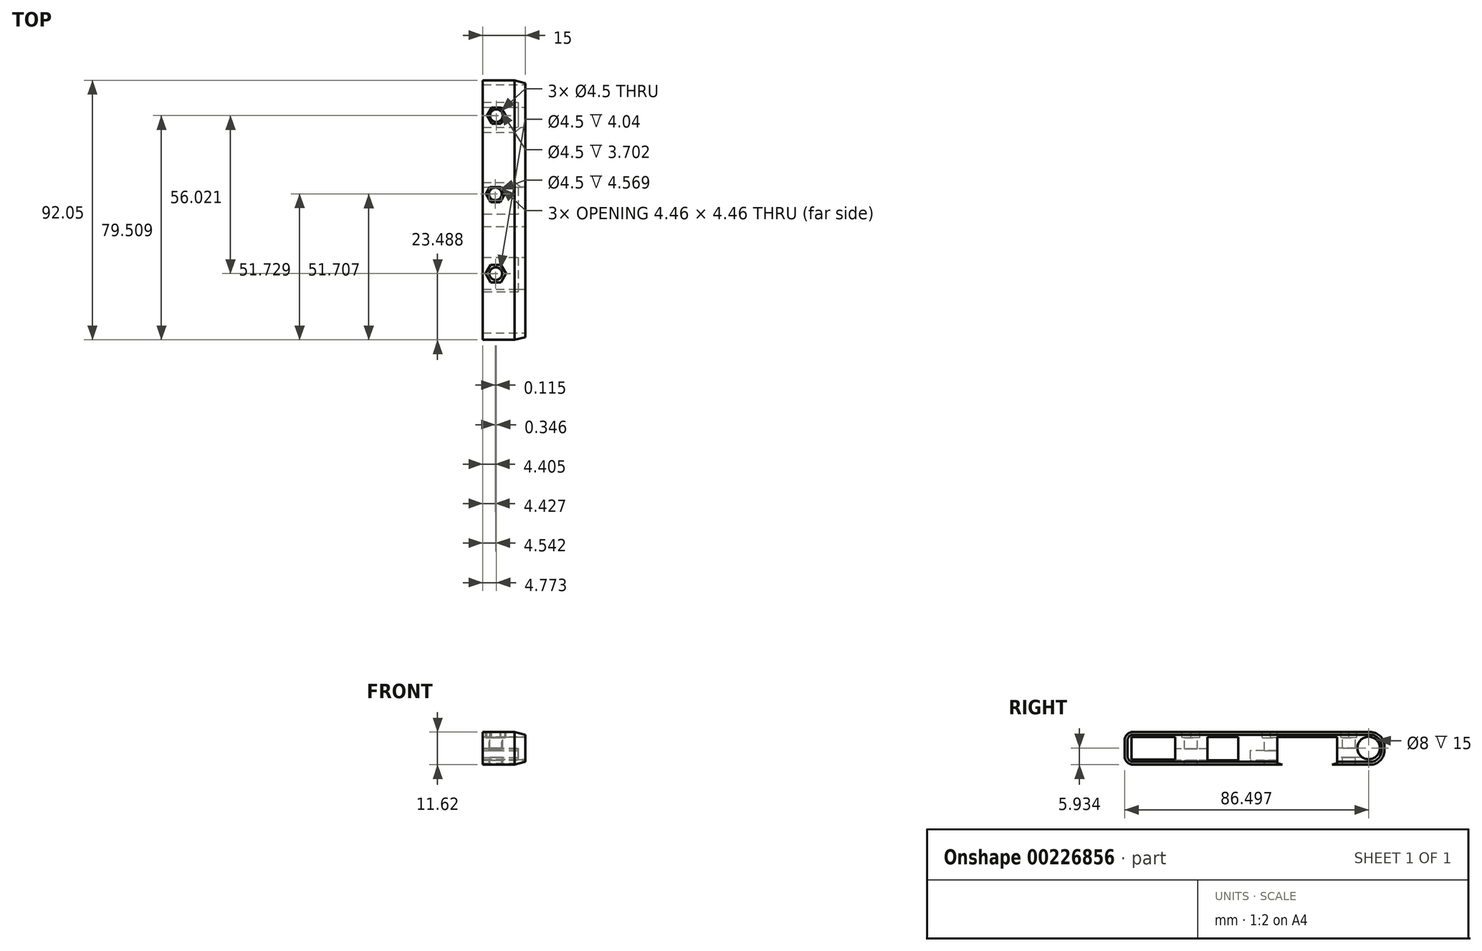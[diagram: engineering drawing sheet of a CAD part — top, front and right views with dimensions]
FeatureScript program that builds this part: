
annotation { "Feature Type Name" : "Feature", "Feature Type Description" : "" }
export const myFeature = defineFeature(function(context is Context, id is Id, definition is map)
    precondition{}
    {
        {
            var Q0;
            Q0=qCreatedBy(makeId("Right.planeOp"),FACE);
            var sketch = newSketch(context, id + "F0", { "sketchPlane" : qUnion([Q0])});
            skLineSegment(sketch, "E0.bottom", {"start": v(42.33, 35.55) * mm, "end": v(-49.72, 35.55) * mm});
            skLineSegment(sketch, "E0.top", {"start": v(42.33, 23.93) * mm, "end": v(-49.72, 23.93) * mm});
            skLineSegment(sketch, "E0.left", {"start": v(42.33, 35.55) * mm, "end": v(42.33, 23.93) * mm});
            skLineSegment(sketch, "E0.right", {"start": v(-49.72, 35.55) * mm, "end": v(-49.72, 23.93) * mm});
            skLineSegment(sketch, "E1.bottom", {"start": v(-31.82, 33.8) * mm, "end": v(-47.32, 33.8) * mm});
            skLineSegment(sketch, "E1.top", {"start": v(-31.82, 25.7) * mm, "end": v(-47.32, 25.7) * mm});
            skLineSegment(sketch, "E1.left", {"start": v(-31.82, 33.8) * mm, "end": v(-31.82, 25.7) * mm});
            skLineSegment(sketch, "E1.right", {"start": v(-47.32, 33.8) * mm, "end": v(-47.32, 25.7) * mm});
            skLineSegment(sketch, "E2.bottom", {"start": v(25.58, 33.8) * mm, "end": v(4.38, 33.8) * mm});
            skLineSegment(sketch, "E2.top", {"start": v(25.58, 23.5) * mm, "end": v(4.38, 23.5) * mm});
            skLineSegment(sketch, "E2.left", {"start": v(25.58, 33.8) * mm, "end": v(25.58, 23.5) * mm});
            skLineSegment(sketch, "E2.right", {"start": v(4.38, 33.8) * mm, "end": v(4.38, 23.5) * mm});
            skCircle(sketch, "E3", {"center": v(36.78, 29.86) * mm, "radius": 4 * mm});
            skLineSegment(sketch, "E4.bottom", {"start": v(-9.52, 33.8) * mm, "end": v(-20.42, 33.8) * mm});
            skLineSegment(sketch, "E4.top", {"start": v(-9.52, 25.5) * mm, "end": v(-20.42, 25.5) * mm});
            skLineSegment(sketch, "E4.left", {"start": v(-9.52, 33.8) * mm, "end": v(-9.52, 25.5) * mm});
            skLineSegment(sketch, "E4.right", {"start": v(-20.42, 33.8) * mm, "end": v(-20.42, 25.5) * mm});
            skLineSegment(sketch, "E5", {"start": v(25.58, 24.5) * mm, "end": v(22.58, 23.5) * mm});
            skLineSegment(sketch, "E6", {"start": v(14.98, 23.5) * mm, "end": v(14.98, 33.8) * mm, "construction": true});
            skLineSegment(sketch, "E7.MirrorCS", {"start": v(4.38, 24.5) * mm, "end": v(7.38, 23.5) * mm});
            skLineSegment(sketch, "E8", {"start": v(25.58, 33.8) * mm, "end": v(37.44, 33.8) * mm, "construction": true});
            skLineSegment(sketch, "E9", {"start": v(4.38, 33.8) * mm, "end": v(-9.52, 33.8) * mm, "construction": true});
            skLineSegment(sketch, "E10", {"start": v(-31.82, 33.8) * mm, "end": v(-20.42, 33.8) * mm, "construction": true});
            skSolve(sketch);
        }
        {
            var Q0;
            Q0=makeQuery(id+"F0.imprint","IMPRINT",FACE,{"disambiguationData":[TD([[makeQuery(id+"F0.imprint","IMPRINT",EDGE,{"derivedFrom":sQuery(id+"F0.wireOp",EDGE,"E0.bottom")}),1.0]])]});
            var Q1;
            {var subQ3=sQuery(id+"F0.wireOp",EDGE,"E7.MirrorCS");Q1=makeQuery(id+"F0.imprint","IMPRINT",FACE,{"disambiguationData":[TD([[makeQuery(id+"F0.imprint","IMPRINT",EDGE,{"derivedFrom":subQ3}),-1.0]])]});}
            var Q2;
            {var subQ3=sQuery(id+"F0.wireOp",EDGE,"E5");Q2=makeQuery(id+"F0.imprint","IMPRINT",FACE,{"disambiguationData":[TD([[makeQuery(id+"F0.imprint","IMPRINT",EDGE,{"derivedFrom":subQ3}),1.0]])]});}
            extrude(context, id + "F1", {"entities" : qUnion([Q0, Q1, Q2]), "oppositeDirection" : true, "depth" : 15 * mm});
        }
        {
            var Q0;
            Q0=makeQuery(id+"F1.opExtrude","CAP_FACE",FACE,{"disambiguationData":[OSD([sQuery(id+"F0.wireOp",EDGE,"E0.bottom"),sQuery(id+"F0.wireOp",EDGE,"E0.top"),sQuery(id+"F0.wireOp",EDGE,"E0.left"),sQuery(id+"F0.wireOp",EDGE,"E0.right"),sQuery(id+"F0.wireOp",EDGE,"E1.bottom"),sQuery(id+"F0.wireOp",EDGE,"E1.top"),sQuery(id+"F0.wireOp",EDGE,"E1.left"),sQuery(id+"F0.wireOp",EDGE,"E1.right"),sQuery(id+"F0.wireOp",EDGE,"E2.bottom"),sQuery(id+"F0.wireOp",EDGE,"E2.top"),sQuery(id+"F0.wireOp",EDGE,"E2.left"),sQuery(id+"F0.wireOp",EDGE,"E2.right"),sQuery(id+"F0.wireOp",EDGE,"E3"),sQuery(id+"F0.wireOp",EDGE,"E4.bottom"),sQuery(id+"F0.wireOp",EDGE,"E4.top"),sQuery(id+"F0.wireOp",EDGE,"E4.left"),sQuery(id+"F0.wireOp",EDGE,"E4.right"),sQuery(id+"F0.wireOp",EDGE,"E5"),sQuery(id+"F0.wireOp",EDGE,"E7.MirrorCS")])],"isStart":false});
            var sketch = newSketch(context, id + "F2", { "sketchPlane" : qUnion([Q0])});
            skLineSegment(sketch, "E11.bottom", {"start": v(-34.86, 29.85) * mm, "end": v(-23.82, 29.85) * mm});
            skLineSegment(sketch, "E11.top", {"start": v(-34.86, 26.55) * mm, "end": v(-23.82, 26.55) * mm});
            skLineSegment(sketch, "E11.left", {"start": v(-34.86, 29.85) * mm, "end": v(-34.86, 26.55) * mm});
            skLineSegment(sketch, "E11.right", {"start": v(-23.82, 29.85) * mm, "end": v(-23.82, 26.55) * mm});
            skLineSegment(sketch, "E12.bottom", {"start": v(-7, 28.98) * mm, "end": v(5.27, 28.98) * mm});
            skLineSegment(sketch, "E12.top", {"start": v(-7, 25.52) * mm, "end": v(5.27, 25.52) * mm});
            skLineSegment(sketch, "E12.left", {"start": v(-7, 28.98) * mm, "end": v(-7, 25.52) * mm});
            skLineSegment(sketch, "E12.right", {"start": v(5.27, 28.98) * mm, "end": v(5.27, 25.52) * mm});
            skLineSegment(sketch, "E13.bottom", {"start": v(18.51, 29.51) * mm, "end": v(32.74, 29.51) * mm});
            skLineSegment(sketch, "E13.top", {"start": v(18.51, 25.52) * mm, "end": v(32.74, 25.52) * mm});
            skLineSegment(sketch, "E13.left", {"start": v(18.51, 29.51) * mm, "end": v(18.51, 25.52) * mm});
            skLineSegment(sketch, "E13.right", {"start": v(32.74, 29.51) * mm, "end": v(32.74, 25.52) * mm});
            skSolve(sketch);
        }
        {
            var Q0;
            Q0 = qSketchRegion(id + "F2", true);
            extrude(context, id + "F3", {"entities" : qUnion([Q0]), "operationType" : NewBodyOperationType.REMOVE, "oppositeDirection" : true, "depth" : 12.5 * mm});
        }
        {
            var Q0;
            Q0=makeQuery(id+"F1.opExtrude","SWEPT_FACE",FACE,{"disambiguationData":[OSD([sQuery(id+"F0.wireOp",EDGE,"E0.bottom")])]});
            var sketch = newSketch(context, id + "F4", { "sketchPlane" : qUnion([Q0])});
            skLineSegment(sketch, "E14.0", {"start": v(-15, 25.58) * mm, "end": v(0, 25.58) * mm});
            skLineSegment(sketch, "E15.0", {"start": v(-15, 4.38) * mm, "end": v(0, 4.38) * mm});
            skLineSegment(sketch, "E16.0", {"start": v(-15, -20.42) * mm, "end": v(0, -20.42) * mm});
            skLineSegment(sketch, "E17.0", {"start": v(-15, -31.82) * mm, "end": v(0, -31.82) * mm});
            skLineSegment(sketch, "E18.0", {"start": v(-15, 32.78) * mm, "end": v(-2.5, 32.78) * mm});
            skCircle(sketch, "E19", {"center": v(-10.23, 29.79) * mm, "radius": 2.25 * mm});
            skLineSegment(sketch, "E20.0", {"start": v(-15, -9.52) * mm, "end": v(0, -9.52) * mm});
            skCircle(sketch, "E21", {"center": v(-10.57, 2) * mm, "radius": 2.25 * mm});
            skCircle(sketch, "E22", {"center": v(-10.46, -26.23) * mm, "radius": 2.25 * mm});
            skCircle(sketch, "E23.cCircle", {"center": v(-10.23, 29.79) * mm, "radius": 2.85 * mm, "construction": true});
            skLineSegment(sketch, "E23.0", {"start": v(-8.58, 26.94) * mm, "end": v(-11.87, 26.94) * mm});
            skLineSegment(sketch, "E23.1", {"start": v(-11.87, 26.94) * mm, "end": v(-13.51, 29.79) * mm});
            skLineSegment(sketch, "E23.2", {"start": v(-13.51, 29.79) * mm, "end": v(-11.87, 32.64) * mm});
            skLineSegment(sketch, "E23.3", {"start": v(-11.87, 32.64) * mm, "end": v(-8.58, 32.64) * mm});
            skLineSegment(sketch, "E23.4", {"start": v(-8.58, 32.64) * mm, "end": v(-6.94, 29.79) * mm});
            skLineSegment(sketch, "E23.5", {"start": v(-6.94, 29.79) * mm, "end": v(-8.58, 26.94) * mm});
            skPoint(sketch, "E23.0.midPoint", {"position": v(-10.23, 26.94) * mm});
            skCircle(sketch, "E24.cCircle", {"center": v(-10.57, 2) * mm, "radius": 2.92 * mm, "construction": true});
            skLineSegment(sketch, "E24.0", {"start": v(-8.89, -0.9) * mm, "end": v(-12.26, -0.9) * mm});
            skLineSegment(sketch, "E24.1", {"start": v(-12.26, -0.9) * mm, "end": v(-13.94, 2) * mm});
            skLineSegment(sketch, "E24.2", {"start": v(-13.94, 2) * mm, "end": v(-12.26, 4.93) * mm});
            skLineSegment(sketch, "E24.3", {"start": v(-12.26, 4.93) * mm, "end": v(-8.89, 4.93) * mm});
            skLineSegment(sketch, "E24.4", {"start": v(-8.89, 4.93) * mm, "end": v(-7.2, 2) * mm});
            skLineSegment(sketch, "E24.5", {"start": v(-7.2, 2) * mm, "end": v(-8.89, -0.9) * mm});
            skPoint(sketch, "E24.0.midPoint", {"position": v(-10.57, -0.9) * mm});
            skCircle(sketch, "E25.cCircle", {"center": v(-10.46, -26.23) * mm, "radius": 3.14 * mm, "construction": true});
            skLineSegment(sketch, "E25.0", {"start": v(-8.65, -29.37) * mm, "end": v(-12.27, -29.37) * mm});
            skLineSegment(sketch, "E25.1", {"start": v(-12.27, -29.37) * mm, "end": v(-14.08, -26.23) * mm});
            skLineSegment(sketch, "E25.2", {"start": v(-14.08, -26.23) * mm, "end": v(-12.27, -23.1) * mm});
            skLineSegment(sketch, "E25.3", {"start": v(-12.27, -23.1) * mm, "end": v(-8.65, -23.1) * mm});
            skLineSegment(sketch, "E25.4", {"start": v(-8.65, -23.1) * mm, "end": v(-6.84, -26.23) * mm});
            skLineSegment(sketch, "E25.5", {"start": v(-6.84, -26.23) * mm, "end": v(-8.65, -29.37) * mm});
            skPoint(sketch, "E25.0.midPoint", {"position": v(-10.46, -29.37) * mm});
            skSolve(sketch);
        }
        {
            var Q0;
            Q0=makeQuery(id+"F4.imprint","IMPRINT",FACE,{"disambiguationData":[TD([[makeQuery(id+"F4.imprint","IMPRINT",EDGE,{"derivedFrom":sQuery(id+"F4.wireOp",EDGE,"E19")}),1.0]])]});
            var Q1;
            Q1=makeQuery(id+"F4.imprint","IMPRINT",FACE,{"disambiguationData":[TD([[makeQuery(id+"F4.imprint","IMPRINT",EDGE,{"derivedFrom":sQuery(id+"F4.wireOp",EDGE,"E21")}),1.0]])]});
            var Q2;
            Q2=makeQuery(id+"F4.imprint","IMPRINT",FACE,{"disambiguationData":[TD([[makeQuery(id+"F4.imprint","IMPRINT",EDGE,{"derivedFrom":sQuery(id+"F4.wireOp",EDGE,"E22")}),1.0]])]});
            extrude(context, id + "F5", {"entities" : qUnion([Q0, Q1, Q2]), "operationType" : NewBodyOperationType.REMOVE, "oppositeDirection" : true, "depth" : 25 * mm});
        }
        {
            var Q0;
            Q0=makeQuery(id+"F4.imprint","IMPRINT",FACE,{"disambiguationData":[TD([[makeQuery(id+"F4.imprint","IMPRINT",EDGE,{"derivedFrom":sQuery(id+"F4.wireOp",EDGE,"E19")}),-1.0]])]});
            var Q1;
            Q1=makeQuery(id+"F4.imprint","IMPRINT",FACE,{"disambiguationData":[TD([[makeQuery(id+"F4.imprint","IMPRINT",EDGE,{"derivedFrom":sQuery(id+"F4.wireOp",EDGE,"E22")}),-1.0]])]});
            var Q2;
            Q2=makeQuery(id+"F4.imprint","IMPRINT",FACE,{"disambiguationData":[TD([[makeQuery(id+"F4.imprint","IMPRINT",EDGE,{"derivedFrom":sQuery(id+"F4.wireOp",EDGE,"E21")}),-1.0]])]});
            extrude(context, id + "F6", {"entities" : qUnion([Q0, Q1, Q2]), "operationType" : NewBodyOperationType.REMOVE, "oppositeDirection" : true, "depth" : 2 * mm});
        }
        {
            var Q0;
            Q0=makeQuery(id+"F1.opExtrude","SWEPT_EDGE",EDGE,{"disambiguationData":[OSD([sQuery(id+"F0.wireOp",EDGE,"E0.top"),sQuery(id+"F0.wireOp",EDGE,"E0.left")])]});
            var Q1;
            Q1=makeQuery(id+"F1.opExtrude","SWEPT_EDGE",EDGE,{"disambiguationData":[OSD([sQuery(id+"F0.wireOp",EDGE,"E0.bottom"),sQuery(id+"F0.wireOp",EDGE,"E0.left")])]});
            fillet(context, id + "F7", {"entities" : qUnion([Q0, Q1]), "radius" : 5 * mm, "tangentPropagation" : true, "allowEdgeOverflow" : false});
        }
        {
            var Q0;
            Q0=makeQuery(id+"F1.opExtrude","SWEPT_EDGE",EDGE,{"disambiguationData":[OSD([sQuery(id+"F0.wireOp",EDGE,"E0.bottom"),sQuery(id+"F0.wireOp",EDGE,"E0.right")])]});
            var Q1;
            Q1=makeQuery(id+"F1.opExtrude","SWEPT_EDGE",EDGE,{"disambiguationData":[OSD([sQuery(id+"F0.wireOp",EDGE,"E0.top"),sQuery(id+"F0.wireOp",EDGE,"E0.right")])]});
            fillet(context, id + "F8", {"entities" : qUnion([Q0, Q1]), "radius" : 3 * mm, "tangentPropagation" : true, "allowEdgeOverflow" : false});
        }
        {
            var Q0;
            Q0=makeQuery(id+"F1.opExtrude","CAP_EDGE",EDGE,{"disambiguationData":[OSD([sQuery(id+"F0.wireOp",EDGE,"E0.bottom")])],"isStart":true});
            chamfer(context, id + "F9", {"entities" : qUnion([Q0]), "chamferType" : ChamferType.OFFSET_ANGLE, "width" : 1 * mm, "oppositeDirection" : false, "angle" : 75 * degree, "tangentPropagation" : true});
        }
    });
